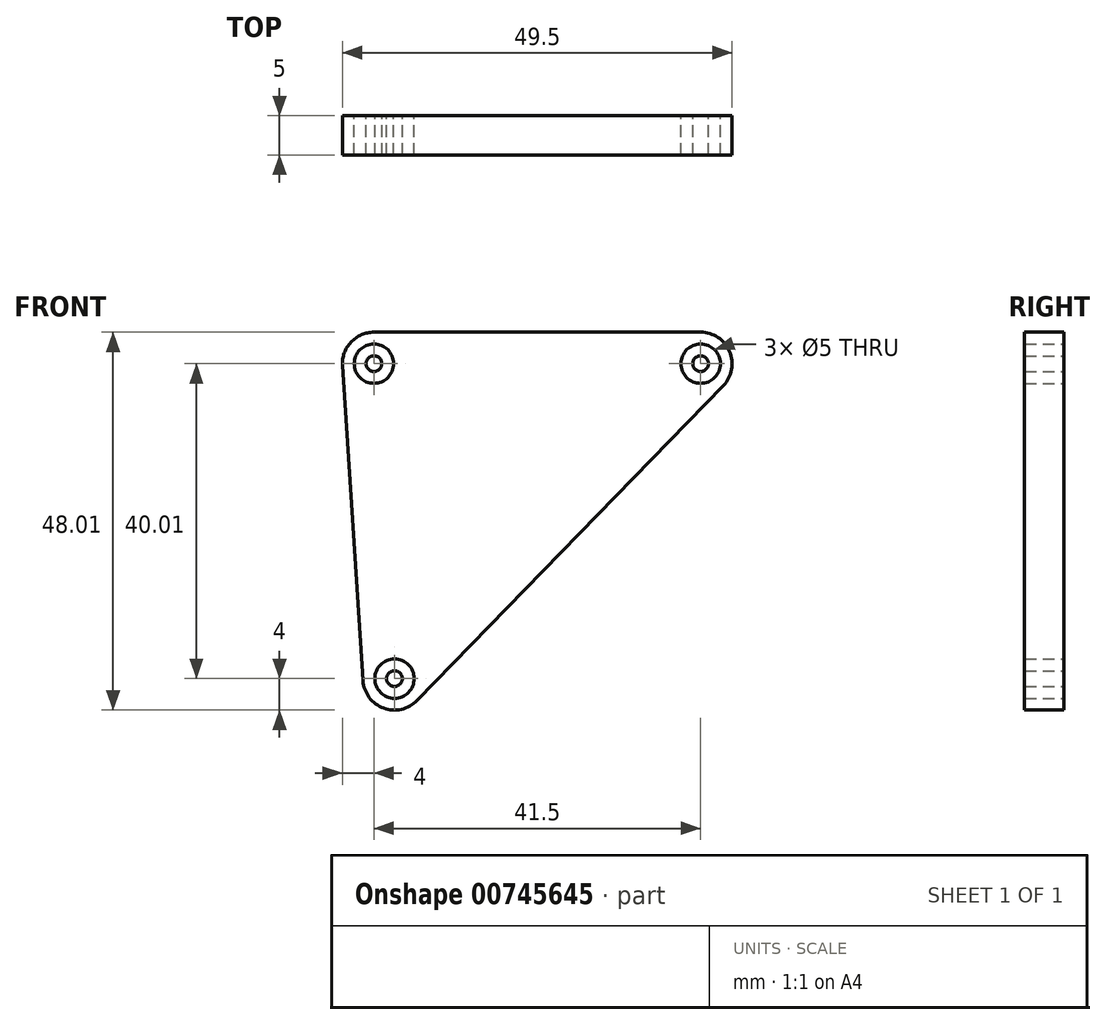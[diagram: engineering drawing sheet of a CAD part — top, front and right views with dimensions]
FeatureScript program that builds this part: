
annotation { "Feature Type Name" : "Feature", "Feature Type Description" : "" }
export const myFeature = defineFeature(function(context is Context, id is Id, definition is map)
    precondition{}
    {
        {
            var Q0;
            Q0=qCreatedBy(makeId("Front.planeOp"),FACE);
            var sketch = newSketch(context, id + "F0", { "sketchPlane" : qUnion([Q0])});
            skLineSegment(sketch, "E0", {"start": v(-19.7, 2.48) * mm, "end": v(-17.1, -37.53) * mm});
            skLineSegment(sketch, "E1", {"start": v(-10.23, -40.06) * mm, "end": v(28.66, -0.05) * mm});
            skLineSegment(sketch, "E2", {"start": v(25.79, 6.74) * mm, "end": v(-15.71, 6.74) * mm});
            skArc(sketch, "E3", {"start": v(-15.71, 6.74) * mm, "mid": v(-18.63, 5.47) * mm, "end": v(-19.7, 2.48) * mm});
            skArc(sketch, "E4", {"start": v(28.66, -0.05) * mm, "mid": v(29.47, 4.3) * mm, "end": v(25.79, 6.74) * mm});
            skArc(sketch, "E5", {"start": v(-17.1, -37.53) * mm, "mid": v(-14.48, -41.02) * mm, "end": v(-10.23, -40.06) * mm});
            skCircle(sketch, "E6", {"center": v(-15.71, 2.74) * mm, "radius": 2.5 * mm});
            skCircle(sketch, "E7", {"center": v(25.79, 2.74) * mm, "radius": 2.5 * mm});
            skCircle(sketch, "E8", {"center": v(-13.1, -37.27) * mm, "radius": 2.5 * mm});
            skCircle(sketch, "E9", {"center": v(-15.71, 2.74) * mm, "radius": 1 * mm});
            skCircle(sketch, "E10", {"center": v(25.79, 2.74) * mm, "radius": 1 * mm});
            skCircle(sketch, "E11", {"center": v(-13.1, -37.27) * mm, "radius": 1 * mm});
            skSolve(sketch);
        }
        {
            var Q0;
            Q0 = qSketchRegion(id + "F0", true);
            var Q1;
            Q1=makeQuery(id+"F0.imprint","IMPRINT",FACE,{"disambiguationData":[TD([[makeQuery(id+"F0.imprint","IMPRINT",EDGE,{"derivedFrom":sQuery(id+"F0.wireOp",EDGE,"E9")}),1.0]])]});
            var Q2;
            Q2=makeQuery(id+"F0.imprint","IMPRINT",FACE,{"disambiguationData":[TD([[makeQuery(id+"F0.imprint","IMPRINT",EDGE,{"derivedFrom":sQuery(id+"F0.wireOp",EDGE,"E10")}),1.0]])]});
            var Q3;
            Q3=makeQuery(id+"F0.imprint","IMPRINT",FACE,{"disambiguationData":[TD([[makeQuery(id+"F0.imprint","IMPRINT",EDGE,{"derivedFrom":sQuery(id+"F0.wireOp",EDGE,"E11")}),1.0]])]});
            extrude(context, id + "F1", {"entities" : qUnion([Q0, Q1, Q2, Q3]), "depth" : 5 * mm, "offsetDistance" : 25 * mm});
        }
    });
